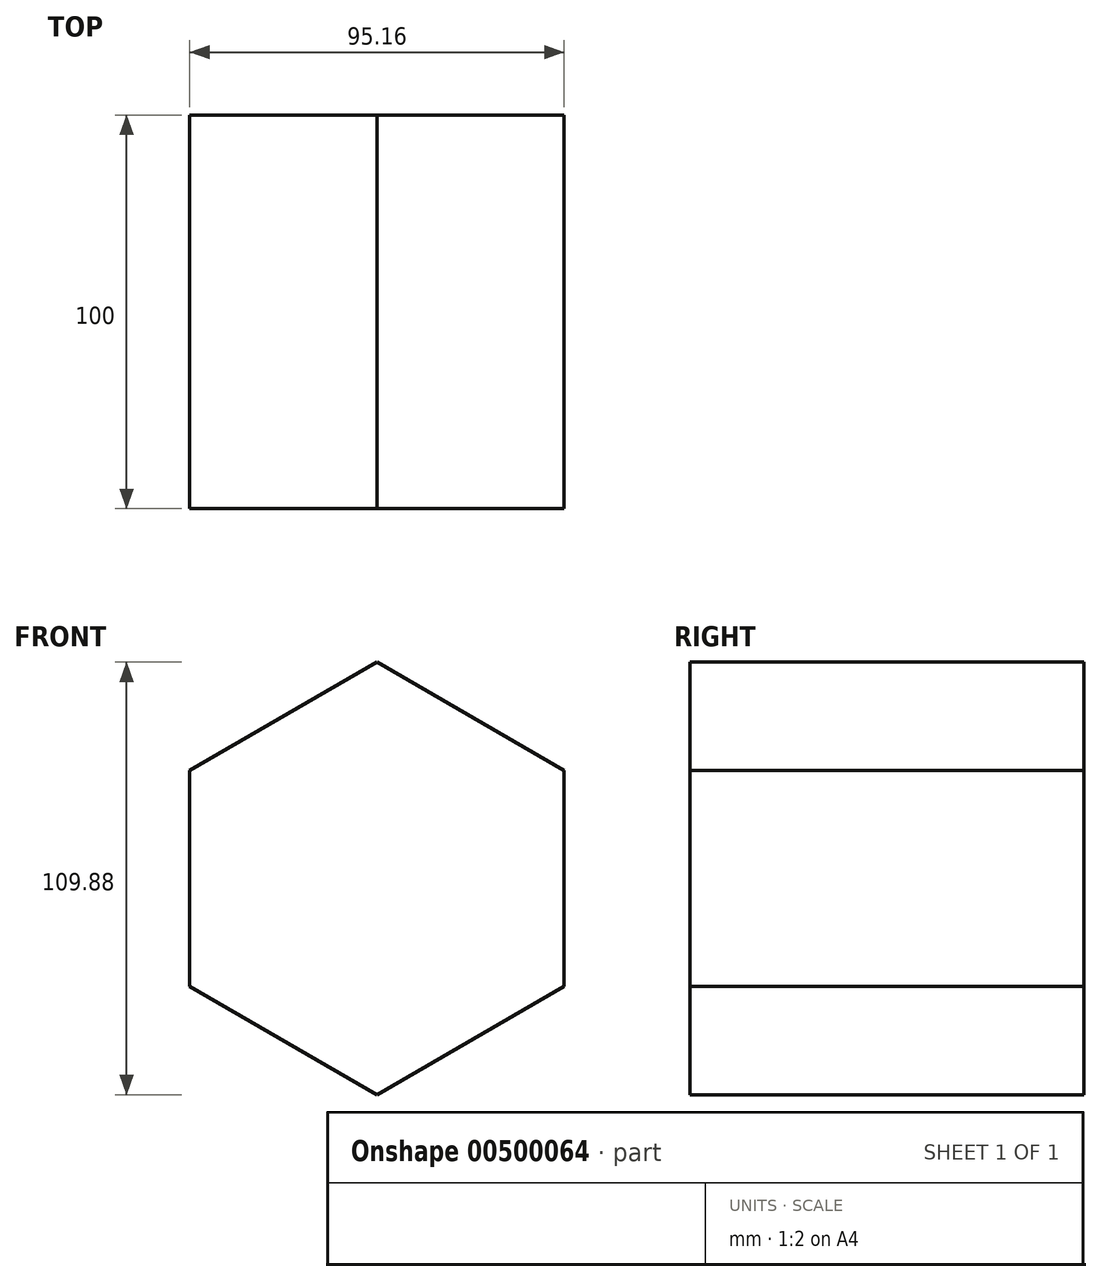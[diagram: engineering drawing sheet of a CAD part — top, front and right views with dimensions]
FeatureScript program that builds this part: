
annotation { "Feature Type Name" : "Feature", "Feature Type Description" : "" }
export const myFeature = defineFeature(function(context is Context, id is Id, definition is map)
    precondition{}
    {
        {
            var Q0;
            Q0=qCreatedBy(makeId("Front.planeOp"),FACE);
            var sketch = newSketch(context, id + "F0", { "sketchPlane" : qUnion([Q0])});
            skCircle(sketch, "E0.cCircle", {"center": v(0, 0) * mm, "radius": 54.94 * mm, "construction": true});
            skLineSegment(sketch, "E0.0", {"start": v(0, 54.94) * mm, "end": v(47.58, 27.47) * mm});
            skLineSegment(sketch, "E0.1", {"start": v(47.58, 27.47) * mm, "end": v(47.58, -27.47) * mm});
            skLineSegment(sketch, "E0.2", {"start": v(47.58, -27.47) * mm, "end": v(0, -54.94) * mm});
            skLineSegment(sketch, "E0.3", {"start": v(0, -54.94) * mm, "end": v(-47.58, -27.47) * mm});
            skLineSegment(sketch, "E0.4", {"start": v(-47.58, -27.47) * mm, "end": v(-47.58, 27.47) * mm});
            skLineSegment(sketch, "E0.5", {"start": v(-47.58, 27.47) * mm, "end": v(0, 54.94) * mm});
            skSolve(sketch);
        }
        {
            var Q0;
            Q0=makeQuery(id+"F0.imprint","IMPRINT",FACE,{"disambiguationData":[TD([[makeQuery(id+"F0.imprint","IMPRINT",EDGE,{"derivedFrom":sQuery(id+"F0.wireOp",EDGE,"E0.0")}),-1.0]])]});
            extrude(context, id + "F1", {"entities" : qUnion([Q0]), "depth" : 100 * mm, "symmetric" : true});
        }
    });
